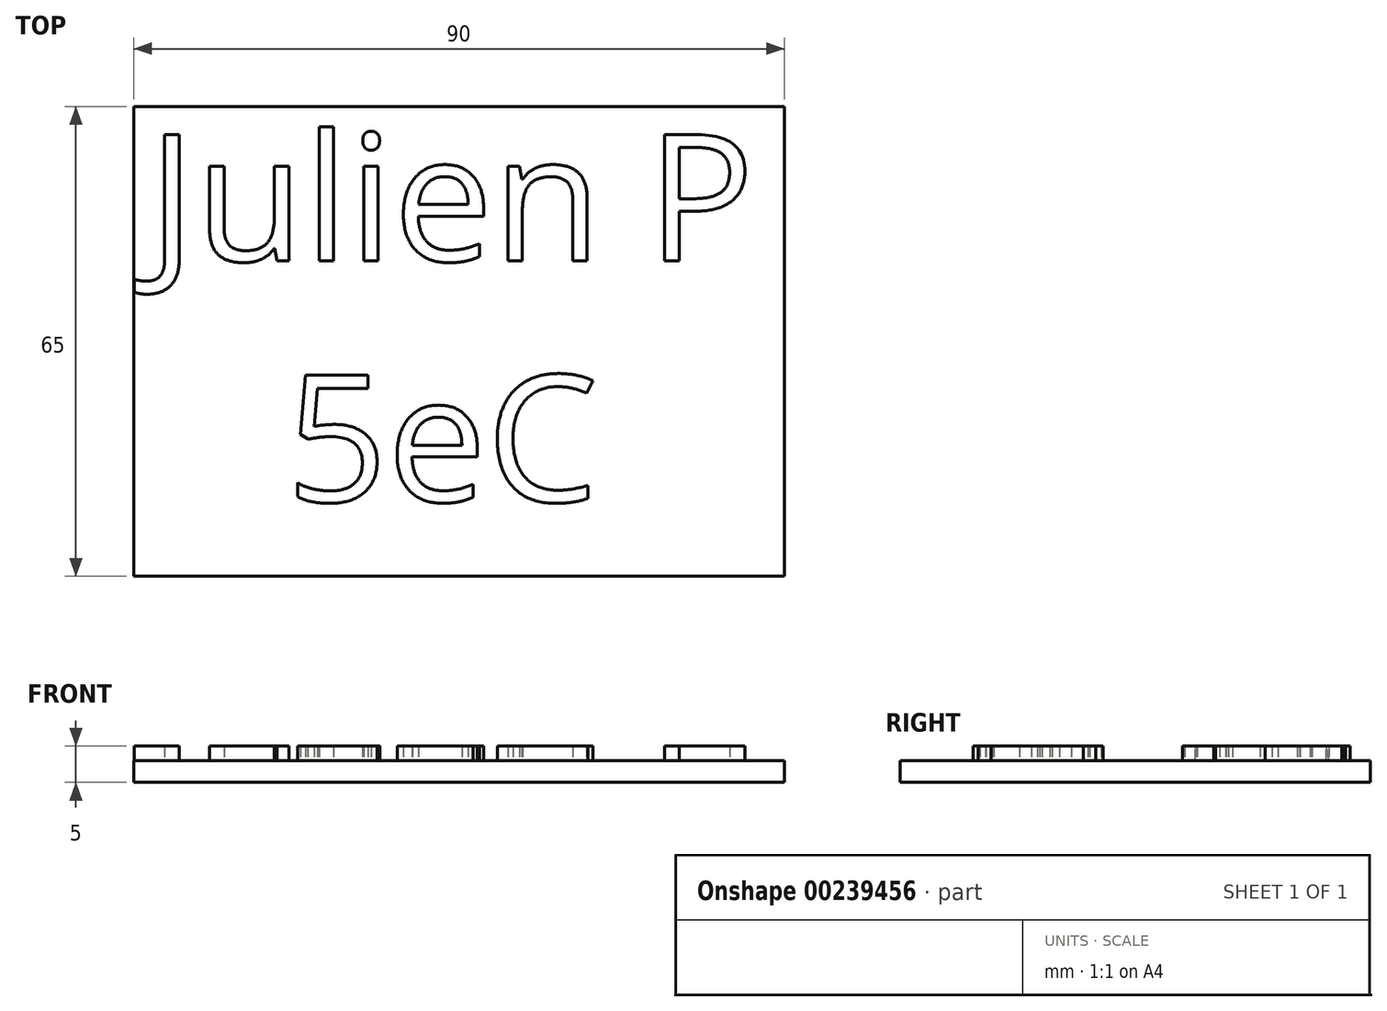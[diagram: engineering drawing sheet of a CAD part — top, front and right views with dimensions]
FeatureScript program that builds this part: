
annotation { "Feature Type Name" : "Feature", "Feature Type Description" : "" }
export const myFeature = defineFeature(function(context is Context, id is Id, definition is map)
    precondition{}
    {
        {
            var Q0;
            Q0=qCreatedBy(makeId("Top.planeOp"),FACE);
            var sketch = newSketch(context, id + "F0", { "sketchPlane" : qUnion([Q0])});
            skLineSegment(sketch, "E0.bottom", {"start": v(0, 0) * mm, "end": v(90, 0) * mm});
            skLineSegment(sketch, "E0.top", {"start": v(0, 65) * mm, "end": v(90, 65) * mm});
            skLineSegment(sketch, "E0.left", {"start": v(0, 0) * mm, "end": v(0, 65) * mm});
            skLineSegment(sketch, "E0.right", {"start": v(90, 0) * mm, "end": v(90, 65) * mm});
            skSolve(sketch);
        }
        {
            var Q0;
            Q0=makeQuery(id+"F0.imprint","IMPRINT",FACE,{"disambiguationData":[TD([[makeQuery(id+"F0.imprint","IMPRINT",EDGE,{"derivedFrom":sQuery(id+"F0.wireOp",EDGE,"E0.bottom")}),1.0]])]});
            extrude(context, id + "F1", {"entities" : qUnion([Q0]), "depth" : 3 * mm});
        }
        {
            var Q0;
            Q0=makeQuery(id+"F1.opExtrude","CAP_FACE",FACE,{"disambiguationData":[OSD([sQuery(id+"F0.wireOp",EDGE,"E0.bottom"),sQuery(id+"F0.wireOp",EDGE,"E0.top"),sQuery(id+"F0.wireOp",EDGE,"E0.left"),sQuery(id+"F0.wireOp",EDGE,"E0.right")])],"isStart":false});
            var sketch = newSketch(context, id + "F2", { "sketchPlane" : qUnion([Q0])});
            skText(sketch, "E1", { "text": "Julien P\n   5eC", "fontName": "OpenSans-Regular.ttf"});
            const initialGuessF2  = {"E1": [0.002, 0.04362, 1, 0, 0.01762]};
            skSetInitialGuess(sketch, initialGuessF2);
            skSolve(sketch);
        }
        {
            var Q0;
            Q0 = qSketchRegion(id + "F2", true);
            extrude(context, id + "F3", {"entities" : qUnion([Q0]), "operationType" : NewBodyOperationType.ADD, "depth" : 2 * mm});
        }
    });
